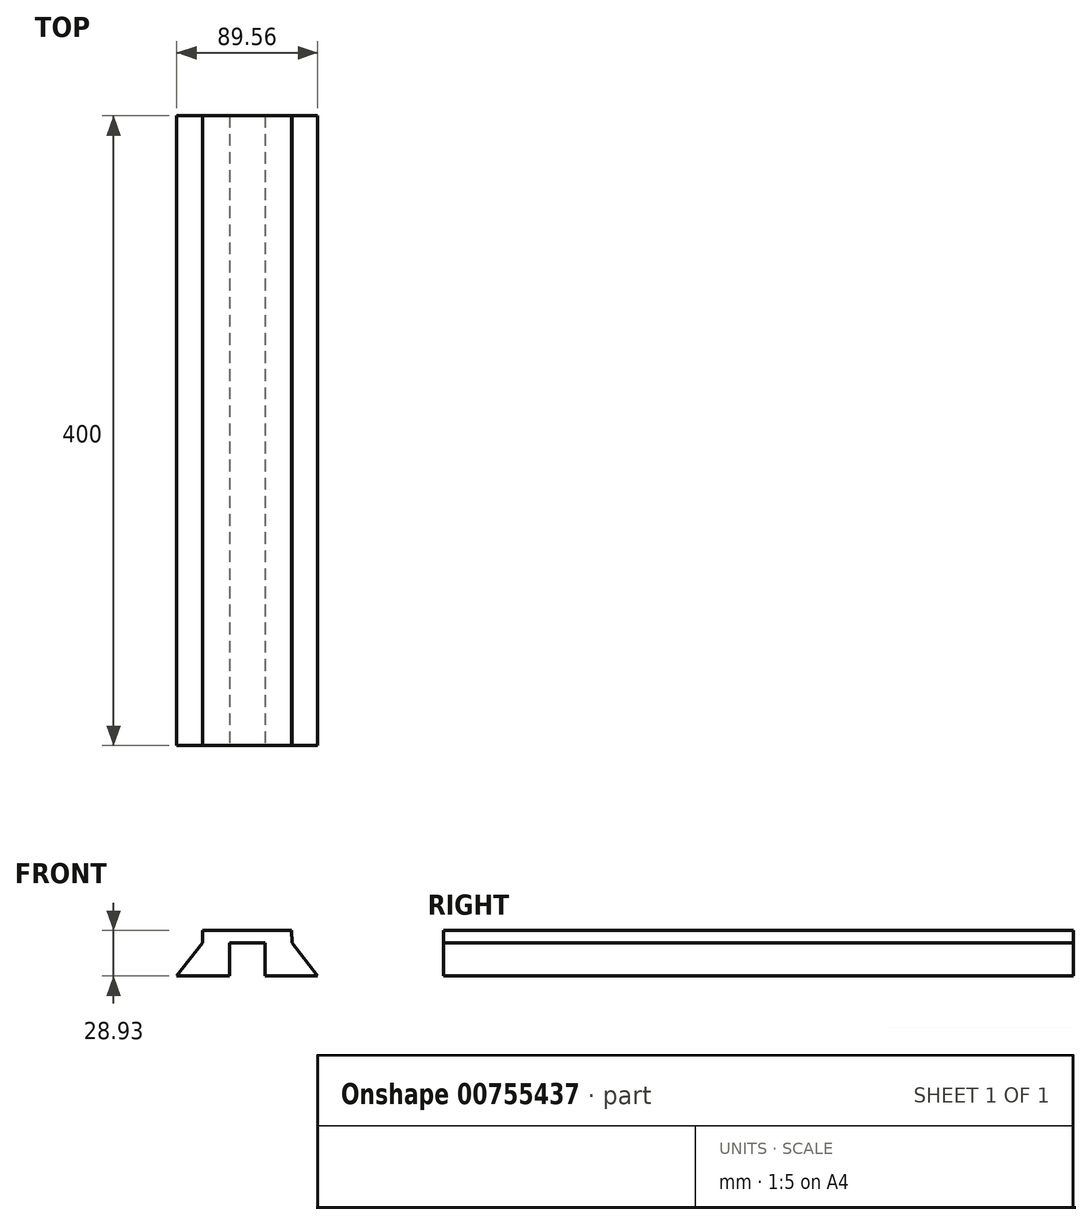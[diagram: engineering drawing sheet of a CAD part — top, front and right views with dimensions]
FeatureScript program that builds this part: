
annotation { "Feature Type Name" : "Feature", "Feature Type Description" : "" }
export const myFeature = defineFeature(function(context is Context, id is Id, definition is map)
    precondition{}
    {
        {
            var Q0;
            Q0=qCreatedBy(makeId("Front.planeOp"),FACE);
            var sketch = newSketch(context, id + "F0", { "sketchPlane" : qUnion([Q0])});
            skLineSegment(sketch, "E0", {"start": v(11.22, 0) * mm, "end": v(28.46, 0) * mm});
            skLineSegment(sketch, "E1", {"start": v(28.46, 20.95) * mm, "end": v(44.78, 0) * mm});
            skLineSegment(sketch, "E2", {"start": v(44.78, 0) * mm, "end": v(28.46, 0) * mm});
            skLineSegment(sketch, "E3", {"start": v(11.22, 20.95) * mm, "end": v(11.22, 0) * mm});
            skLineSegment(sketch, "E4.MirrorCS", {"start": v(-44.78, 0) * mm, "end": v(-28.46, 0) * mm});
            skLineSegment(sketch, "E5.MirrorCS", {"start": v(-28.46, 20.95) * mm, "end": v(-44.78, 0) * mm});
            skLineSegment(sketch, "E6.MirrorCS", {"start": v(-11.22, 20.95) * mm, "end": v(-11.22, 0) * mm});
            skLineSegment(sketch, "E7", {"start": v(-28.46, 0) * mm, "end": v(-11.22, 0) * mm});
            skLineSegment(sketch, "E8", {"start": v(-28.46, 20.95) * mm, "end": v(-28.46, 28.93) * mm});
            skLineSegment(sketch, "E9", {"start": v(-28.46, 28.93) * mm, "end": v(28.28, 28.93) * mm});
            skLineSegment(sketch, "E10", {"start": v(28.28, 28.93) * mm, "end": v(28.46, 20.95) * mm});
            skLineSegment(sketch, "E11", {"start": v(-28.46, 20.95) * mm, "end": v(-28.46, 20.95) * mm});
            skLineSegment(sketch, "E12.trimOffspring", {"start": v(-11.22, 20.95) * mm, "end": v(11.22, 20.95) * mm});
            skSolve(sketch);
        }
        {
            var Q0;
            Q0=makeQuery(id+"F0.imprint","IMPRINT",FACE,{"disambiguationData":[TD([[makeQuery(id+"F0.imprint","IMPRINT",EDGE,{"derivedFrom":sQuery(id+"F0.wireOp",EDGE,"Hx0LAOsT-oL59-Mt75-Yp9e-liyGgY5KFBQ0")}),-1.0]])]});
            var Q1;
            Q1=makeQuery(id+"F0.imprint","IMPRINT",FACE,{"disambiguationData":[TD([[makeQuery(id+"F0.imprint","IMPRINT",EDGE,{"derivedFrom":sQuery(id+"F0.wireOp",EDGE,"E0")}),1.0]])]});
            extrude(context, id + "F1", {"entities" : qUnion([Q0, Q1]), "oppositeDirection" : true, "depth" : 400 * mm, "offsetDistance" : 25.4 * mm});
        }
    });
